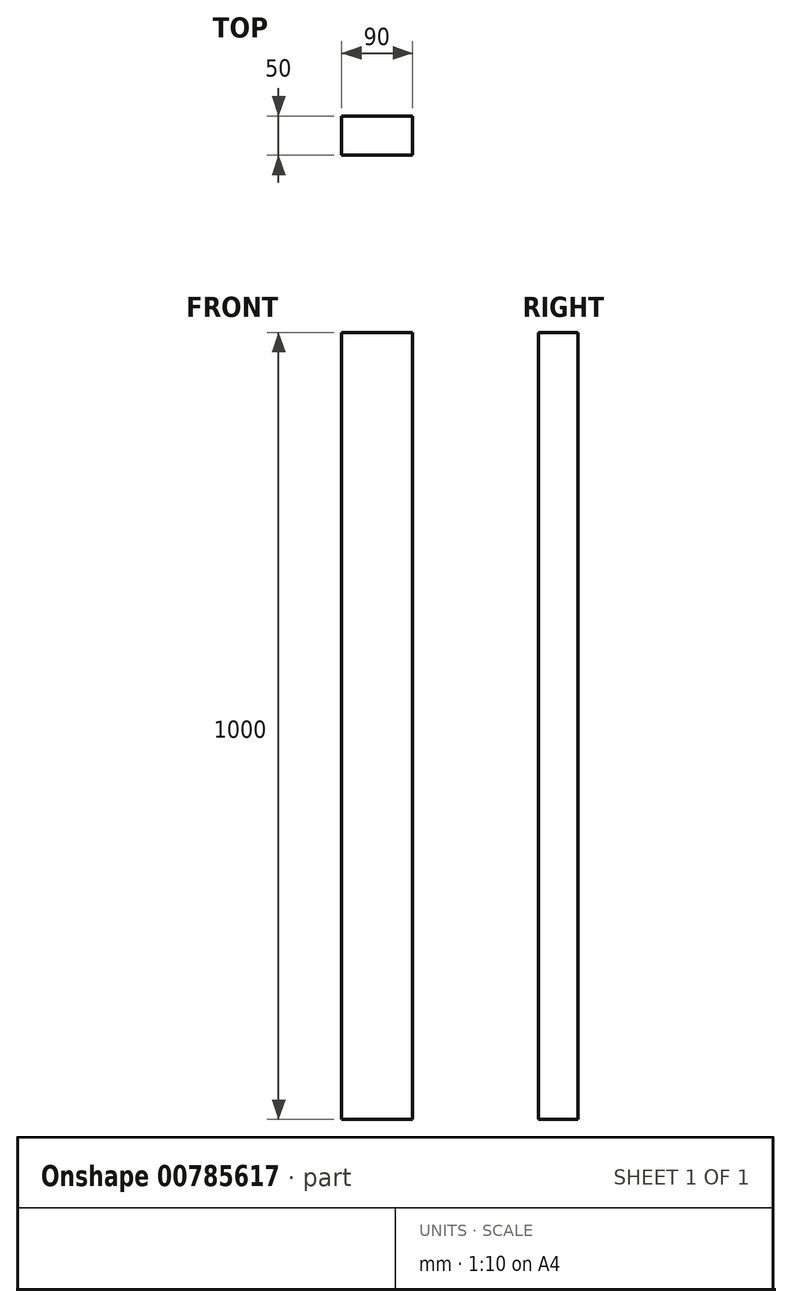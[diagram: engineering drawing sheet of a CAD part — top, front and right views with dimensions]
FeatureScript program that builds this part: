
annotation { "Feature Type Name" : "Feature", "Feature Type Description" : "" }
export const myFeature = defineFeature(function(context is Context, id is Id, definition is map)
    precondition{}
    {
        {
            var Q0;
            Q0=qCreatedBy(makeId("Top.planeOp"),FACE);
            var sketch = newSketch(context, id + "F0", { "sketchPlane" : qUnion([Q0])});
            skLineSegment(sketch, "E0", {"start": v(-50.99, 42.02) * mm, "end": v(39.01, 42.02) * mm});
            skLineSegment(sketch, "E1", {"start": v(39.01, 42.02) * mm, "end": v(39.01, -7.98) * mm});
            skLineSegment(sketch, "E2", {"start": v(39.01, -7.98) * mm, "end": v(-50.99, -7.98) * mm});
            skLineSegment(sketch, "E3", {"start": v(-50.99, 42.02) * mm, "end": v(-50.99, -7.98) * mm});
            skSolve(sketch);
        }
        {
            var Q0;
            Q0=makeQuery(id+"F0.imprint","IMPRINT",FACE,{"disambiguationData":[TD([[makeQuery(id+"F0.imprint","IMPRINT",EDGE,{"derivedFrom":sQuery(id+"F0.wireOp",EDGE,"E0")}),-1.0]])]});
            extrude(context, id + "F1", {"entities" : qUnion([Q0]), "depth" : 1000 * mm, "offsetDistance" : 25 * mm});
        }
    });
